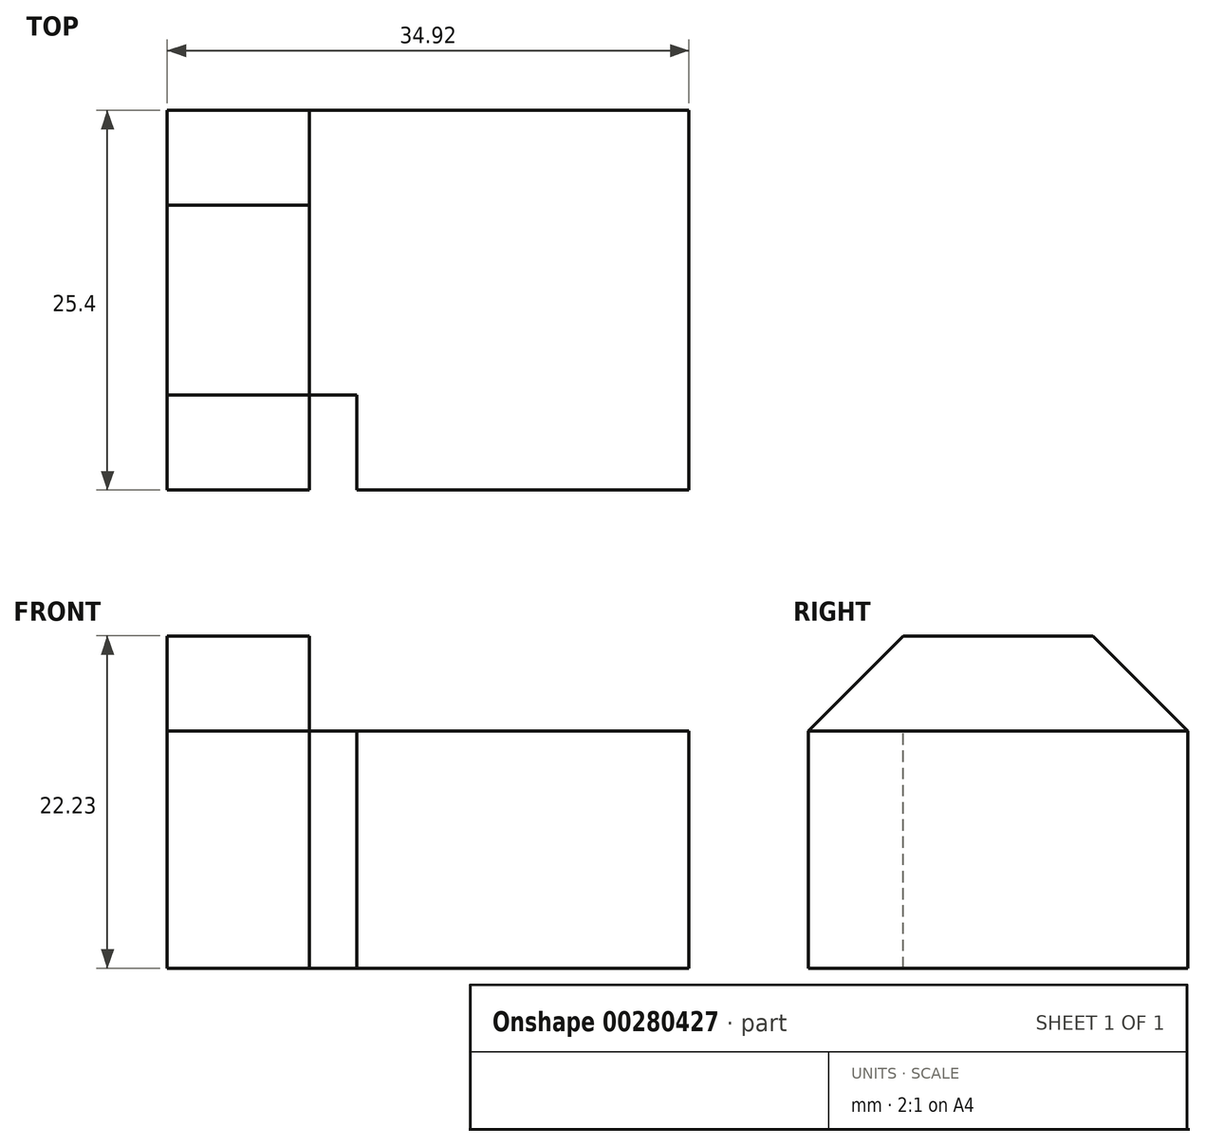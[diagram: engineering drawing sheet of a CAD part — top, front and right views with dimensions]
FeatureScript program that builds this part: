
annotation { "Feature Type Name" : "Feature", "Feature Type Description" : "" }
export const myFeature = defineFeature(function(context is Context, id is Id, definition is map)
    precondition{}
    {
        {
            var Q0;
            Q0=qCreatedBy(makeId("Front.planeOp"),FACE);
            var sketch = newSketch(context, id + "F0", { "sketchPlane" : qUnion([Q0])});
            skLineSegment(sketch, "E0", {"start": v(0, 0) * mm, "end": v(34.93, 0) * mm});
            skLineSegment(sketch, "E1", {"start": v(34.93, 0) * mm, "end": v(34.93, 22.23) * mm});
            skLineSegment(sketch, "E2", {"start": v(34.93, 22.23) * mm, "end": v(0, 22.23) * mm});
            skLineSegment(sketch, "E3", {"start": v(0, 22.23) * mm, "end": v(0, 0) * mm});
            skSolve(sketch);
        }
        {
            var Q0;
            Q0 = qSketchRegion(id + "F0", true);
            extrude(context, id + "F1", {"entities" : qUnion([Q0]), "depth" : 25.4 * mm, "symmetric" : true});
        }
        {
            var Q0;
            Q0=makeQuery(id+"F1.opExtrude","SWEPT_FACE",FACE,{"disambiguationData":[OSD([sQuery(id+"F0.wireOp",EDGE,"E3")])]});
            var sketch = newSketch(context, id + "F2", { "sketchPlane" : qUnion([Q0])});
            skLineSegment(sketch, "E4", {"start": v(12.7, 22.23) * mm, "end": v(12.7, 15.88) * mm});
            skLineSegment(sketch, "E5", {"start": v(12.7, 15.88) * mm, "end": v(6.35, 22.23) * mm});
            skLineSegment(sketch, "E6", {"start": v(6.35, 22.23) * mm, "end": v(12.7, 22.23) * mm});
            skSolve(sketch);
        }
        {
            var Q0;
            Q0 = qSketchRegion(id + "F2", true);
            extrude(context, id + "F3", {"entities" : qUnion([Q0]), "operationType" : NewBodyOperationType.REMOVE, "endBound" : BoundingType.THROUGH_ALL, "oppositeDirection" : true, "depth" : 25.4 * mm});
        }
        {
            var Q0;
            Q0=makeQuery(id+"F1.opExtrude","SWEPT_FACE",FACE,{"disambiguationData":[OSD([sQuery(id+"F0.wireOp",EDGE,"E1")])]});
            var sketch = newSketch(context, id + "F4", { "sketchPlane" : qUnion([Q0])});
            skLineSegment(sketch, "E7", {"start": v(-12.7, 15.88) * mm, "end": v(12.7, 15.88) * mm});
            skLineSegment(sketch, "E8", {"start": v(12.7, 15.88) * mm, "end": v(12.7, 22.23) * mm});
            skLineSegment(sketch, "E9", {"start": v(12.7, 22.23) * mm, "end": v(-6.35, 22.23) * mm});
            skLineSegment(sketch, "E10", {"start": v(-6.35, 22.23) * mm, "end": v(-12.7, 15.88) * mm});
            skSolve(sketch);
        }
        {
            var Q0;
            Q0 = qSketchRegion(id + "F4", true);
            extrude(context, id + "F5", {"entities" : qUnion([Q0]), "operationType" : NewBodyOperationType.REMOVE, "oppositeDirection" : true, "depth" : 25.4 * mm});
        }
        {
            var Q0;
            Q0=makeQuery(id+"F1.opExtrude","SWEPT_FACE",FACE,{"disambiguationData":[OSD([sQuery(id+"F0.wireOp",EDGE,"E3")])]});
            var sketch = newSketch(context, id + "F6", { "sketchPlane" : qUnion([Q0])});
            skLineSegment(sketch, "E11", {"start": v(-12.7, 22.23) * mm, "end": v(-12.7, 15.88) * mm});
            skLineSegment(sketch, "E12", {"start": v(-12.7, 15.87) * mm, "end": v(-6.35, 22.23) * mm});
            skLineSegment(sketch, "E13", {"start": v(-6.35, 22.23) * mm, "end": v(-12.7, 22.23) * mm});
            skSolve(sketch);
        }
        {
            var Q0;
            Q0 = qSketchRegion(id + "F6", true);
            extrude(context, id + "F7", {"entities" : qUnion([Q0]), "operationType" : NewBodyOperationType.REMOVE, "endBound" : BoundingType.THROUGH_ALL, "oppositeDirection" : true, "depth" : 25.4 * mm});
        }
        {
            var Q0;
            Q0=makeQuery(id+"F5.boolean.opBoolean","COPY",FACE,{"derivedFrom":makeQuery(id+"F5.opExtrude","SWEPT_FACE",FACE,{"disambiguationData":[OSD([sQuery(id+"F4.wireOp",EDGE,"E7")])]})});
            var sketch = newSketch(context, id + "F8", { "sketchPlane" : qUnion([Q0])});
            skLineSegment(sketch, "E14", {"start": v(9.53, -12.7) * mm, "end": v(12.7, -12.7) * mm});
            skLineSegment(sketch, "E15", {"start": v(12.7, -12.7) * mm, "end": v(12.7, -6.35) * mm});
            skLineSegment(sketch, "E16", {"start": v(12.7, -6.35) * mm, "end": v(9.53, -6.35) * mm});
            skLineSegment(sketch, "E17", {"start": v(9.53, -6.35) * mm, "end": v(9.53, -12.7) * mm});
            skSolve(sketch);
        }
        {
            var Q0;
            Q0 = qSketchRegion(id + "F8", true);
            extrude(context, id + "F9", {"entities" : qUnion([Q0]), "operationType" : NewBodyOperationType.REMOVE, "endBound" : BoundingType.THROUGH_ALL, "oppositeDirection" : true, "depth" : 25.4 * mm});
        }
    });
